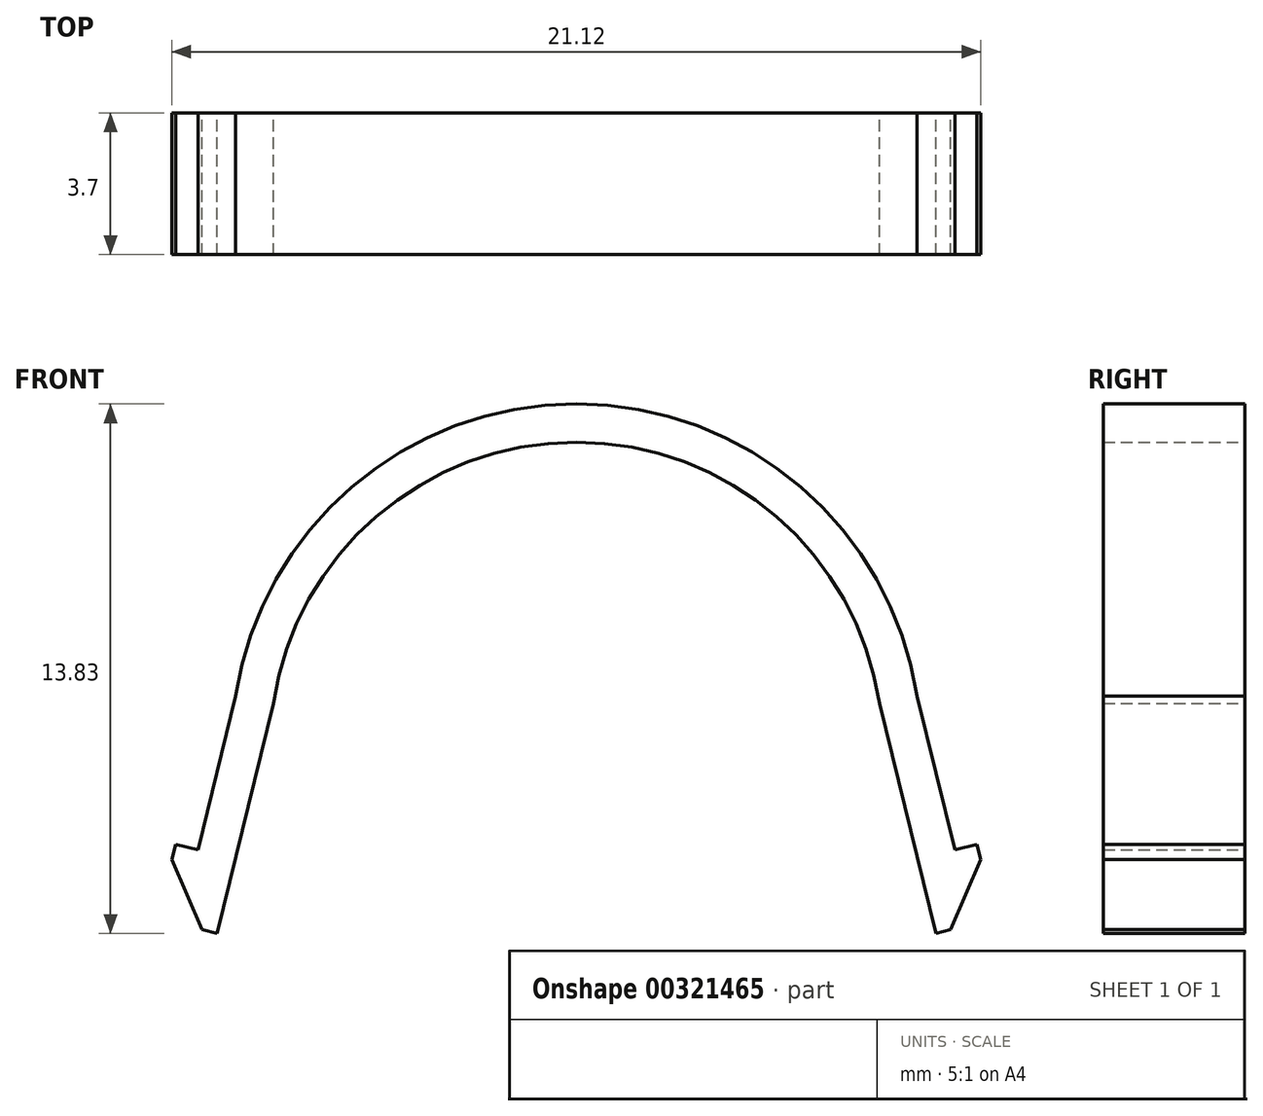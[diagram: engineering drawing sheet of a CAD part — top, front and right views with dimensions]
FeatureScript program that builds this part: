
annotation { "Feature Type Name" : "Feature", "Feature Type Description" : "" }
export const myFeature = defineFeature(function(context is Context, id is Id, definition is map)
    precondition{}
    {
        {
            var Q0;
            Q0=qCreatedBy(makeId("Front.planeOp"),FACE);
            var sketch = newSketch(context, id + "F0", { "sketchPlane" : qUnion([Q0])});
            skLineSegment(sketch, "E0", {"start": v(-9, 0) * mm, "end": v(-9, 2.6) * mm, "construction": true});
            skArc(sketch, "E1", {"start": v(0, 11.6) * mm, "mid": v(-6.36, 8.96) * mm, "end": v(-9, 2.6) * mm});
            skLineSegment(sketch, "E2", {"start": v(0, 38.36) * mm, "end": v(0, -11) * mm, "construction": true});
            skArc(sketch, "E3.0", {"start": v(0, 10.6) * mm, "mid": v(-5.66, 8.26) * mm, "end": v(-8, 2.6) * mm});
            skLineSegment(sketch, "E3.1", {"start": v(-8, -0.41) * mm, "end": v(-8, 2.6) * mm, "construction": true});
            skLineSegment(sketch, "E4", {"start": v(0, 11.6) * mm, "end": v(0, 10.6) * mm});
            skLineSegment(sketch, "E5", {"start": v(-9, 0) * mm, "end": v(-9.6, 0) * mm});
            skLineSegment(sketch, "E6", {"start": v(-9.6, 0) * mm, "end": v(-9.6, -0.5) * mm});
            skLineSegment(sketch, "E7", {"start": v(-9.6, -0.5) * mm, "end": v(-8.5, -1.8) * mm});
            skLineSegment(sketch, "E8", {"start": v(-8.5, -1.8) * mm, "end": v(-8, -1.8) * mm});
            skLineSegment(sketch, "E9", {"start": v(-8, -1.8) * mm, "end": v(-8, -0.41) * mm});
            skLineSegment(sketch, "E10", {"start": v(-8.9, 3.98) * mm, "end": v(-9.88, -0.05) * mm});
            skLineSegment(sketch, "E11.0", {"start": v(-7.91, 3.78) * mm, "end": v(-9.38, -2.23) * mm});
            skLineSegment(sketch, "E12", {"start": v(-10.46, 0.1) * mm, "end": v(-9.88, -0.05) * mm});
            skLineSegment(sketch, "E13", {"start": v(-10.46, 0.1) * mm, "end": v(-10.56, -0.3) * mm});
            skLineSegment(sketch, "E14", {"start": v(-10.56, -0.3) * mm, "end": v(-9.77, -2.13) * mm});
            skLineSegment(sketch, "E15", {"start": v(-9.77, -2.13) * mm, "end": v(-9.38, -2.23) * mm});
            skLineSegment(sketch, "E16.MirrorCS", {"start": v(8.5, -1.8) * mm, "end": v(8, -1.8) * mm});
            skLineSegment(sketch, "E17.MirrorCS", {"start": v(10.46, 0.1) * mm, "end": v(9.88, -0.05) * mm});
            skLineSegment(sketch, "E18.MirrorCS", {"start": v(10.46, 0.1) * mm, "end": v(10.56, -0.3) * mm});
            skLineSegment(sketch, "E19.MirrorCS", {"start": v(9, 0) * mm, "end": v(9.6, 0) * mm});
            skLineSegment(sketch, "E20.MirrorCS", {"start": v(9.6, 0) * mm, "end": v(9.6, -0.5) * mm});
            skLineSegment(sketch, "E21.MirrorCS", {"start": v(9.77, -2.13) * mm, "end": v(9.38, -2.23) * mm});
            skArc(sketch, "E22.MirrorCS", {"start": v(0, 11.6) * mm, "mid": v(6.36, 8.96) * mm, "end": v(9, 2.6) * mm});
            skLineSegment(sketch, "E23.MirrorCS", {"start": v(7.91, 3.78) * mm, "end": v(9.38, -2.23) * mm});
            skArc(sketch, "E24.MirrorCS", {"start": v(0, 10.6) * mm, "mid": v(5.66, 8.26) * mm, "end": v(8, 2.6) * mm});
            skLineSegment(sketch, "E25.MirrorCS", {"start": v(10.56, -0.3) * mm, "end": v(9.77, -2.13) * mm});
            skLineSegment(sketch, "E26.MirrorCS", {"start": v(8.9, 3.98) * mm, "end": v(9.88, -0.05) * mm});
            skLineSegment(sketch, "E27.MirrorCS", {"start": v(9.6, -0.5) * mm, "end": v(8.5, -1.8) * mm});
            skLineSegment(sketch, "E28.MirrorCS", {"start": v(9, 0) * mm, "end": v(9, 2.6) * mm, "construction": true});
            skLineSegment(sketch, "E29.MirrorCS", {"start": v(8, -0.41) * mm, "end": v(8, 2.6) * mm, "construction": true});
            skLineSegment(sketch, "E30.MirrorCS", {"start": v(8, -1.8) * mm, "end": v(8, -0.41) * mm});
            skSolve(sketch);
        }
        {
            var Q0;
            Q0 = qSketchRegion(id + "F0", true);
            extrude(context, id + "F1", {"entities" : qUnion([Q0]), "depth" : 3.7 * mm});
        }
    });
